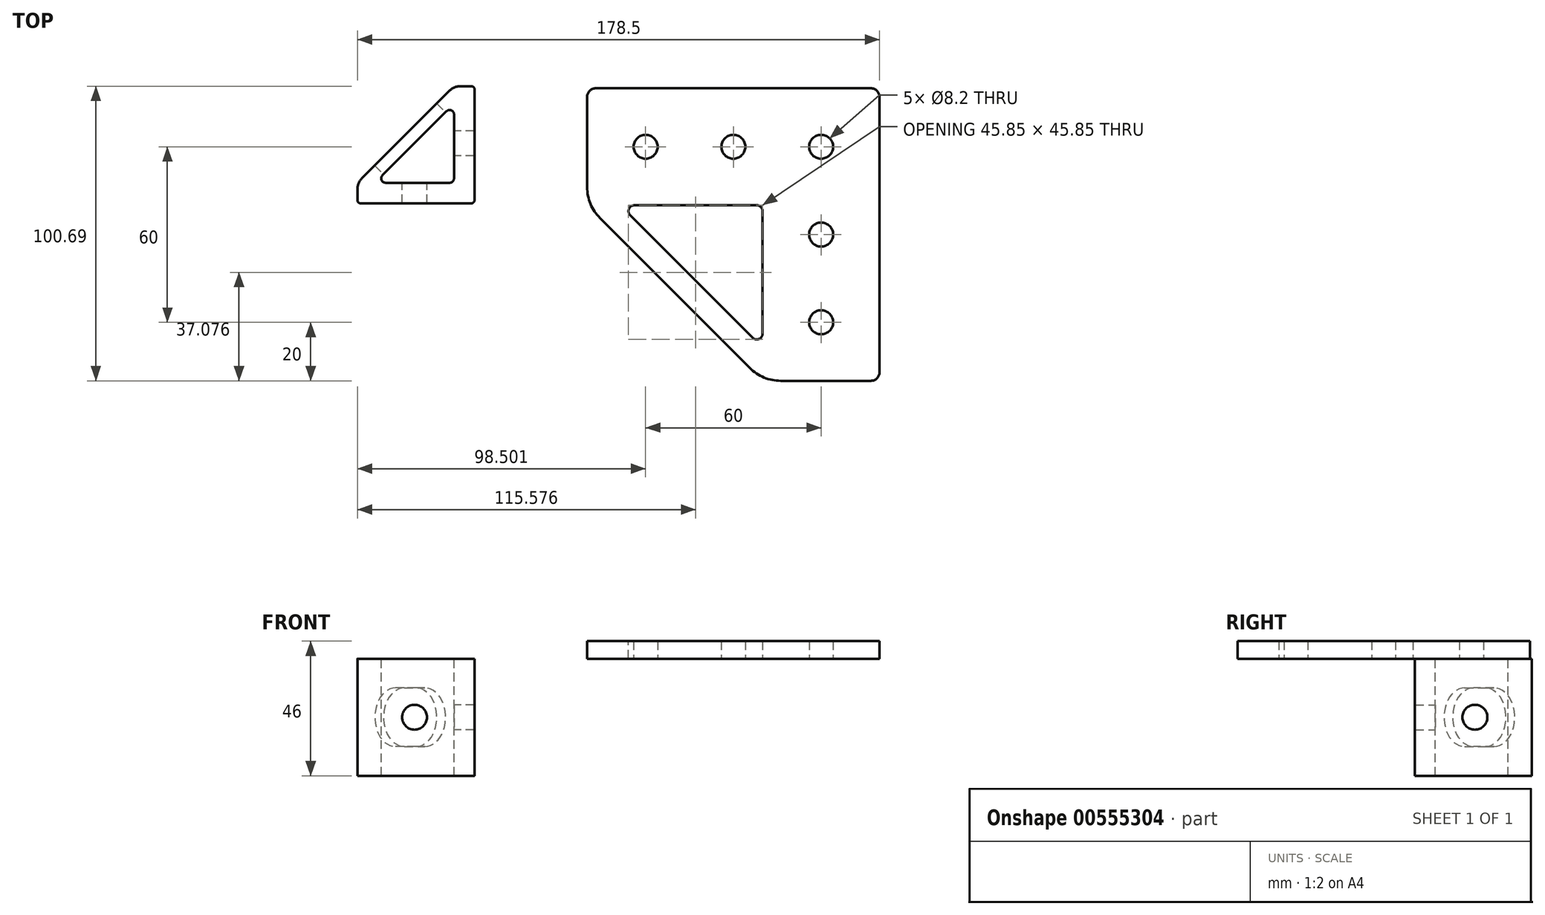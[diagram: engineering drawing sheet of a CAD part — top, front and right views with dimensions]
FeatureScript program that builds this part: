
annotation { "Feature Type Name" : "Feature", "Feature Type Description" : "" }
export const myFeature = defineFeature(function(context is Context, id is Id, definition is map)
    precondition{}
    {
        {
            var Q0;
            Q0=qCreatedBy(makeId("Top.planeOp"),FACE);
            var sketch = newSketch(context, id + "F0", { "sketchPlane" : qUnion([Q0])});
            skLineSegment(sketch, "E0.bottom", {"start": v(78.5, 20) * mm, "end": v(-21.5, 20) * mm});
            skLineSegment(sketch, "E0.top", {"start": v(78.5, -80) * mm, "end": v(38.5, -80) * mm});
            skLineSegment(sketch, "E0.left", {"start": v(78.5, 20) * mm, "end": v(78.5, -80) * mm});
            skLineSegment(sketch, "E0.right", {"start": v(-21.5, 20) * mm, "end": v(-21.5, -20) * mm});
            skLineSegment(sketch, "E1", {"start": v(-21.5, -20) * mm, "end": v(38.5, -80) * mm});
            skCircle(sketch, "E2", {"center": v(-1.5, 0) * mm, "radius": 4.1 * mm});
            skCircle(sketch, "E3.1.0.0", {"center": v(28.5, 0) * mm, "radius": 4.1 * mm});
            skCircle(sketch, "E3.2.0.0", {"center": v(58.5, 0) * mm, "radius": 4.1 * mm});
            skLineSegment(sketch, "E3.direction1", {"start": v(-1.5, 0) * mm, "end": v(28.5, 0) * mm, "construction": true});
            skCircle(sketch, "E4.0.1.0", {"center": v(58.5, -30) * mm, "radius": 4.1 * mm});
            skLineSegment(sketch, "E4.direction1", {"start": v(58.5, 0) * mm, "end": v(83, 0) * mm, "construction": true});
            skLineSegment(sketch, "E4.direction2", {"start": v(58.5, 0) * mm, "end": v(58.5, -30) * mm, "construction": true});
            skCircle(sketch, "E5.0.0.2", {"center": v(58.5, -60) * mm, "radius": 4.1 * mm});
            skLineSegment(sketch, "E6.top", {"start": v(-21.5, -20) * mm, "end": v(38.5, -20) * mm});
            skLineSegment(sketch, "E6.right", {"start": v(38.5, -80) * mm, "end": v(38.5, -20) * mm});
            skLineSegment(sketch, "E7.bottom", {"start": v(-60, -19.31) * mm, "end": v(-100, -19.31) * mm});
            skLineSegment(sketch, "E7.top", {"start": v(-60, 20.69) * mm, "end": v(-100, 20.69) * mm});
            skLineSegment(sketch, "E7.left", {"start": v(-60, -19.31) * mm, "end": v(-60, 20.69) * mm});
            skLineSegment(sketch, "E7.right", {"start": v(-100, -19.31) * mm, "end": v(-100, 20.69) * mm});
            skLineSegment(sketch, "E8", {"start": v(-100, -18.31) * mm, "end": v(-61, 20.69) * mm});
            skLineSegment(sketch, "E9", {"start": v(-100, -12.31) * mm, "end": v(-67, 20.69) * mm});
            skLineSegment(sketch, "E10", {"start": v(-100, -12.31) * mm, "end": v(-67, -12.31) * mm});
            skLineSegment(sketch, "E11", {"start": v(-67, -12.31) * mm, "end": v(-67, 20.69) * mm});
            skLineSegment(sketch, "E12", {"start": v(38.5, -68.69) * mm, "end": v(-10.19, -20) * mm});
            skSolve(sketch);
        }
        {
            var Q0;
            Q0=makeQuery(id+"F0.imprint","IMPRINT",FACE,{"disambiguationData":[TD([[makeQuery(id+"F0.imprint","IMPRINT",EDGE,{"derivedFrom":makeQuery(id+"FnEUytPFRcbeFGa_0.opExtrude","CAP_EDGE",EDGE,{"disambiguationData":[OSD([sQuery(id+"F1H9fzjYB6yz2IO_0.wireOp",EDGE,"PCZt6Eaf-3QD0-oKbU-Kmi7-AaeVj3FxadjA.top")])],"isStart":false})}),1.0]])]});
            var Q1;
            {var subQ1=makeQuery(id+"FnEUytPFRcbeFGa_0.opExtrude","CAP_EDGE",EDGE,{"disambiguationData":[OSD([sQuery(id+"F1H9fzjYB6yz2IO_0.wireOp",EDGE,"2f640ecb-bae4-4474-8c9a-e0769f365833.3.0")])],"isStart":false});Q1=makeQuery(id+"F0.imprint","IMPRINT",FACE,{"disambiguationData":[TD([[makeQuery(id+"F0.imprint","IMPRINT",EDGE,{"derivedFrom":subQ1}),1.0]])]});}
            var Q2;
            Q2=makeQuery(id+"F0.imprint","IMPRINT",FACE,{"disambiguationData":[TD([[makeQuery(id+"F0.imprint","IMPRINT",EDGE,{"derivedFrom":sQuery(id+"F0.wireOp",EDGE,"E3.2.0.0")}),-1.0]])]});
            var Q3;
            {var subQ3=sQuery(id+"F0.wireOp",EDGE,"E1");Q3=makeQuery(id+"F0.imprint","IMPRINT",FACE,{"disambiguationData":[TD([[makeQuery(id+"F0.imprint","IMPRINT",EDGE,{"derivedFrom":subQ3}),1.0]])]});}
            extrude(context, id + "F1", {"entities" : qUnion([Q0, Q1, Q2, Q3]), "depth" : 6 * mm, "offsetDistance" : 25 * mm});
        }
        {
            var Q0;
            {var subQ5=sQuery(id+"F0.wireOp",EDGE,"E7.bottom");Q0=makeQuery(id+"F0.imprint","IMPRINT",FACE,{"disambiguationData":[TD([[makeQuery(id+"F0.imprint","IMPRINT",EDGE,{"derivedFrom":subQ5}),-1.0]])]});}
            var Q1;
            {var subQ0=sQuery(id+"F0.wireOp",EDGE,"E8");var subQ1=sQuery(id+"F0.wireOp",EDGE,"E7.right");var subQ2=makeQuery(id+"F0.imprint","INTERSECT",VERTEX,{"derivedFrom":[subQ1,subQ0]});Q1=makeQuery(id+"F0.imprint","IMPRINT",FACE,{"disambiguationData":[TD([[makeQuery(id+"F0.imprint","IMPRINT",EDGE,{"disambiguationData":[TD([[subQ2,-1.0]])],"derivedFrom":subQ0}),1.0]])]});}
            var Q2;
            {var subQ5=sQuery(id+"F0.wireOp",EDGE,"E9");Q2=makeQuery(id+"F0.imprint","IMPRINT",FACE,{"disambiguationData":[TD([[makeQuery(id+"F0.imprint","IMPRINT",EDGE,{"derivedFrom":subQ5}),-1.0]])]});}
            var Q3;
            {var subQ0=sQuery(id+"F0.wireOp",EDGE,"E8");var subQ1=sQuery(id+"F0.wireOp",EDGE,"E7.top");var subQ2=makeQuery(id+"F0.imprint","INTERSECT",VERTEX,{"derivedFrom":[subQ1,subQ0]});Q3=makeQuery(id+"F0.imprint","IMPRINT",FACE,{"disambiguationData":[TD([[makeQuery(id+"F0.imprint","IMPRINT",EDGE,{"disambiguationData":[TD([[subQ2,1.0]])],"derivedFrom":subQ0}),1.0]])]});}
            extrude(context, id + "F2", {"entities" : qUnion([Q0, Q1, Q2, Q3]), "oppositeDirection" : true, "depth" : 40 * mm, "offsetDistance" : 25 * mm});
        }
        {
            var Q0;
            Q0=makeQuery(id+"F2.opExtrude","SWEPT_FACE",FACE,{"disambiguationData":[OSD([sQuery(id+"F0.wireOp",EDGE,"E10")])]});
            var sketch = newSketch(context, id + "F3", { "sketchPlane" : qUnion([Q0])});
            skCircle(sketch, "E13", {"center": v(80.5, -20) * mm, "radius": 4.25 * mm});
            skSolve(sketch);
        }
        {
            var Q0;
            Q0=makeQuery(id+"F2.opExtrude","SWEPT_FACE",FACE,{"disambiguationData":[OSD([sQuery(id+"F0.wireOp",EDGE,"E11")])]});
            var sketch = newSketch(context, id + "F4", { "sketchPlane" : qUnion([Q0])});
            skCircle(sketch, "E14", {"center": v(-1.19, -20) * mm, "radius": 4.25 * mm});
            skSolve(sketch);
        }
        {
            var Q0;
            Q0=sQuery(id+"F4.wireOp",VERTEX,"E14.center");
            var Q1;
            Q1=sQuery(id+"F3.wireOp",VERTEX,"E13.center");
            var Q2;
            Q2=makeQuery(id+"F2.opExtrude","SWEPT_BODY",BODY,{"disambiguationData":[OSD([sQuery(id+"F0.wireOp",EDGE,"E7.bottom"),sQuery(id+"F0.wireOp",EDGE,"E7.top"),sQuery(id+"F0.wireOp",EDGE,"E7.left"),sQuery(id+"F0.wireOp",EDGE,"E7.right"),sQuery(id+"F0.wireOp",EDGE,"E8"),sQuery(id+"F0.wireOp",EDGE,"E9"),sQuery(id+"F0.wireOp",EDGE,"E10"),sQuery(id+"F0.wireOp",EDGE,"E11")])]});
            hole(context, id + "F5", {"style" : HoleStyle.SIMPLE, "endStyle" : HoleEndStyle.BLIND, "holeDiameter" : 8.5 * mm, "majorDiameter" : 5 * mm, "holeDepth" : 28 * mm, "isTappedThrough" : true, "tappedDepth" : 12 * mm, "tapClearance" : 3, "locations" : qUnion([Q0, Q1]), "scope" : qUnion([Q2])});
        }
        {
            var Q0;
            Q0=makeQuery(id+"F2.opExtrude","SWEPT_FACE",FACE,{"disambiguationData":[OSD([sQuery(id+"F0.wireOp",EDGE,"E9")])]});
            var sketch = newSketch(context, id + "F6", { "sketchPlane" : qUnion([Q0])});
            skLineSegment(sketch, "E15.bottom", {"start": v(41.05, -10) * mm, "end": v(71.05, -10) * mm});
            skLineSegment(sketch, "E15.top", {"start": v(41.05, -30) * mm, "end": v(71.05, -30) * mm});
            skLineSegment(sketch, "E15.left", {"start": v(41.05, -10) * mm, "end": v(41.05, -30) * mm});
            skLineSegment(sketch, "E15.right", {"start": v(71.05, -10) * mm, "end": v(71.05, -30) * mm});
            skPoint(sketch, "E15.middle", {"position": v(56.05, -20) * mm});
            skSolve(sketch);
        }
        {
            var Q0;
            Q0 = qSketchRegion(id + "F6", true);
            extrude(context, id + "F7", {"entities" : qUnion([Q0]), "operationType" : NewBodyOperationType.REMOVE, "oppositeDirection" : true, "depth" : 5 * mm, "offsetDistance" : 25 * mm});
        }
        {
            var Q0;
            Q0=makeQuery(id+"F7.boolean.opBoolean","COPY",EDGE,{"derivedFrom":makeQuery(id+"F7.opExtrude","SWEPT_EDGE",EDGE,{"disambiguationData":[OSD([sQuery(id+"F6.wireOp",EDGE,"E15.bottom"),sQuery(id+"F6.wireOp",EDGE,"E15.right")])]})});
            var Q1;
            Q1=makeQuery(id+"F7.boolean.opBoolean","COPY",EDGE,{"derivedFrom":makeQuery(id+"F7.opExtrude","SWEPT_EDGE",EDGE,{"disambiguationData":[OSD([sQuery(id+"F6.wireOp",EDGE,"E15.top"),sQuery(id+"F6.wireOp",EDGE,"E15.right")])]})});
            var Q2;
            Q2=makeQuery(id+"F7.boolean.opBoolean","COPY",EDGE,{"derivedFrom":makeQuery(id+"F7.opExtrude","SWEPT_EDGE",EDGE,{"disambiguationData":[OSD([sQuery(id+"F6.wireOp",EDGE,"E15.top"),sQuery(id+"F6.wireOp",EDGE,"E15.left")])]})});
            var Q3;
            Q3=makeQuery(id+"F7.boolean.opBoolean","COPY",EDGE,{"derivedFrom":makeQuery(id+"F7.opExtrude","SWEPT_EDGE",EDGE,{"disambiguationData":[OSD([sQuery(id+"F6.wireOp",EDGE,"E15.bottom"),sQuery(id+"F6.wireOp",EDGE,"E15.left")])]})});
            fillet(context, id + "F8", {"entities" : qUnion([Q0, Q1, Q2, Q3]), "radius" : 10 * mm, "tangentPropagation" : true, "allowEdgeOverflow" : false});
        }
        {
            var Q0;
            Q0=makeQuery(id+"F2.opExtrude","SWEPT_EDGE",EDGE,{"disambiguationData":[OSD([sQuery(id+"F0.wireOp",EDGE,"E7.top"),sQuery(id+"F0.wireOp",EDGE,"E9"),sQuery(id+"F0.wireOp",EDGE,"E11")])]});
            var Q1;
            Q1=makeQuery(id+"F2.opExtrude","SWEPT_EDGE",EDGE,{"disambiguationData":[OSD([sQuery(id+"F0.wireOp",EDGE,"E7.right"),sQuery(id+"F0.wireOp",EDGE,"E9"),sQuery(id+"F0.wireOp",EDGE,"E10")])]});
            fillet(context, id + "F9", {"entities" : qUnion([Q0, Q1]), "radius" : 5 * mm, "tangentPropagation" : true, "allowEdgeOverflow" : false});
        }
        {
            var Q0;
            Q0=makeQuery(id+"F2.opExtrude","SWEPT_EDGE",EDGE,{"disambiguationData":[OSD([sQuery(id+"F0.wireOp",EDGE,"E8"),sQuery(id+"F0.wireOp",EDGE,"E11")])]});
            var Q1;
            Q1=makeQuery(id+"F2.opExtrude","SWEPT_EDGE",EDGE,{"disambiguationData":[OSD([sQuery(id+"F0.wireOp",EDGE,"E10"),sQuery(id+"F0.wireOp",EDGE,"E11")])]});
            var Q2;
            Q2=makeQuery(id+"F2.opExtrude","SWEPT_EDGE",EDGE,{"disambiguationData":[OSD([sQuery(id+"F0.wireOp",EDGE,"E8"),sQuery(id+"F0.wireOp",EDGE,"E10")])]});
            fillet(context, id + "F10", {"entities" : qUnion([Q0, Q1, Q2]), "radius" : 1.5 * mm, "tangentPropagation" : true, "allowEdgeOverflow" : false});
        }
        {
            var Q0;
            Q0=makeQuery(id+"F2.opExtrude","SWEPT_EDGE",EDGE,{"disambiguationData":[OSD([sQuery(id+"F0.wireOp",EDGE,"E7.top"),sQuery(id+"F0.wireOp",EDGE,"E7.left")])]});
            var Q1;
            Q1=makeQuery(id+"F2.opExtrude","SWEPT_EDGE",EDGE,{"disambiguationData":[OSD([sQuery(id+"F0.wireOp",EDGE,"E7.bottom"),sQuery(id+"F0.wireOp",EDGE,"E7.right")])]});
            var Q2;
            Q2=makeQuery(id+"F2.opExtrude","SWEPT_EDGE",EDGE,{"disambiguationData":[OSD([sQuery(id+"F0.wireOp",EDGE,"E7.bottom"),sQuery(id+"F0.wireOp",EDGE,"E7.left")])]});
            fillet(context, id + "F11", {"entities" : qUnion([Q0, Q1, Q2]), "radius" : 1 * mm, "tangentPropagation" : true, "allowEdgeOverflow" : false});
        }
        {
            var Q0;
            Q0=makeQuery(id+"F1.opExtrude","SWEPT_EDGE",EDGE,{"disambiguationData":[OSD([sQuery(id+"F0.wireOp",EDGE,"E0.top"),sQuery(id+"F0.wireOp",EDGE,"E1"),sQuery(id+"F0.wireOp",EDGE,"E6.right")])]});
            var Q1;
            Q1=makeQuery(id+"F1.opExtrude","SWEPT_EDGE",EDGE,{"disambiguationData":[OSD([sQuery(id+"F0.wireOp",EDGE,"E0.right"),sQuery(id+"F0.wireOp",EDGE,"E1"),sQuery(id+"F0.wireOp",EDGE,"E6.top")])]});
            fillet(context, id + "F12", {"entities" : qUnion([Q0, Q1]), "radius" : 15 * mm, "tangentPropagation" : true, "allowEdgeOverflow" : false});
        }
        {
            var Q0;
            Q0=makeQuery(id+"F1.opExtrude","SWEPT_EDGE",EDGE,{"disambiguationData":[OSD([sQuery(id+"F0.wireOp",EDGE,"E6.top"),sQuery(id+"F0.wireOp",EDGE,"E6.right")])]});
            var Q1;
            Q1=makeQuery(id+"F1.opExtrude","SWEPT_EDGE",EDGE,{"disambiguationData":[OSD([sQuery(id+"F0.wireOp",EDGE,"E6.top"),sQuery(id+"F0.wireOp",EDGE,"E12")])]});
            var Q2;
            Q2=makeQuery(id+"F1.opExtrude","SWEPT_EDGE",EDGE,{"disambiguationData":[OSD([sQuery(id+"F0.wireOp",EDGE,"E6.right"),sQuery(id+"F0.wireOp",EDGE,"E12")])]});
            fillet(context, id + "F13", {"entities" : qUnion([Q0, Q1, Q2]), "radius" : 2 * mm, "tangentPropagation" : true, "allowEdgeOverflow" : false});
        }
        {
            var Q0;
            Q0=makeQuery(id+"F1.opExtrude","SWEPT_EDGE",EDGE,{"disambiguationData":[OSD([sQuery(id+"F0.wireOp",EDGE,"E0.bottom"),sQuery(id+"F0.wireOp",EDGE,"E0.right")])]});
            var Q1;
            Q1=makeQuery(id+"F1.opExtrude","SWEPT_EDGE",EDGE,{"disambiguationData":[OSD([sQuery(id+"F0.wireOp",EDGE,"E0.bottom"),sQuery(id+"F0.wireOp",EDGE,"E0.left")])]});
            var Q2;
            Q2=makeQuery(id+"F1.opExtrude","SWEPT_EDGE",EDGE,{"disambiguationData":[OSD([sQuery(id+"F0.wireOp",EDGE,"E0.top"),sQuery(id+"F0.wireOp",EDGE,"E0.left")])]});
            fillet(context, id + "F14", {"entities" : qUnion([Q0, Q1, Q2]), "radius" : 3 * mm, "tangentPropagation" : true, "allowEdgeOverflow" : false});
        }
    });
